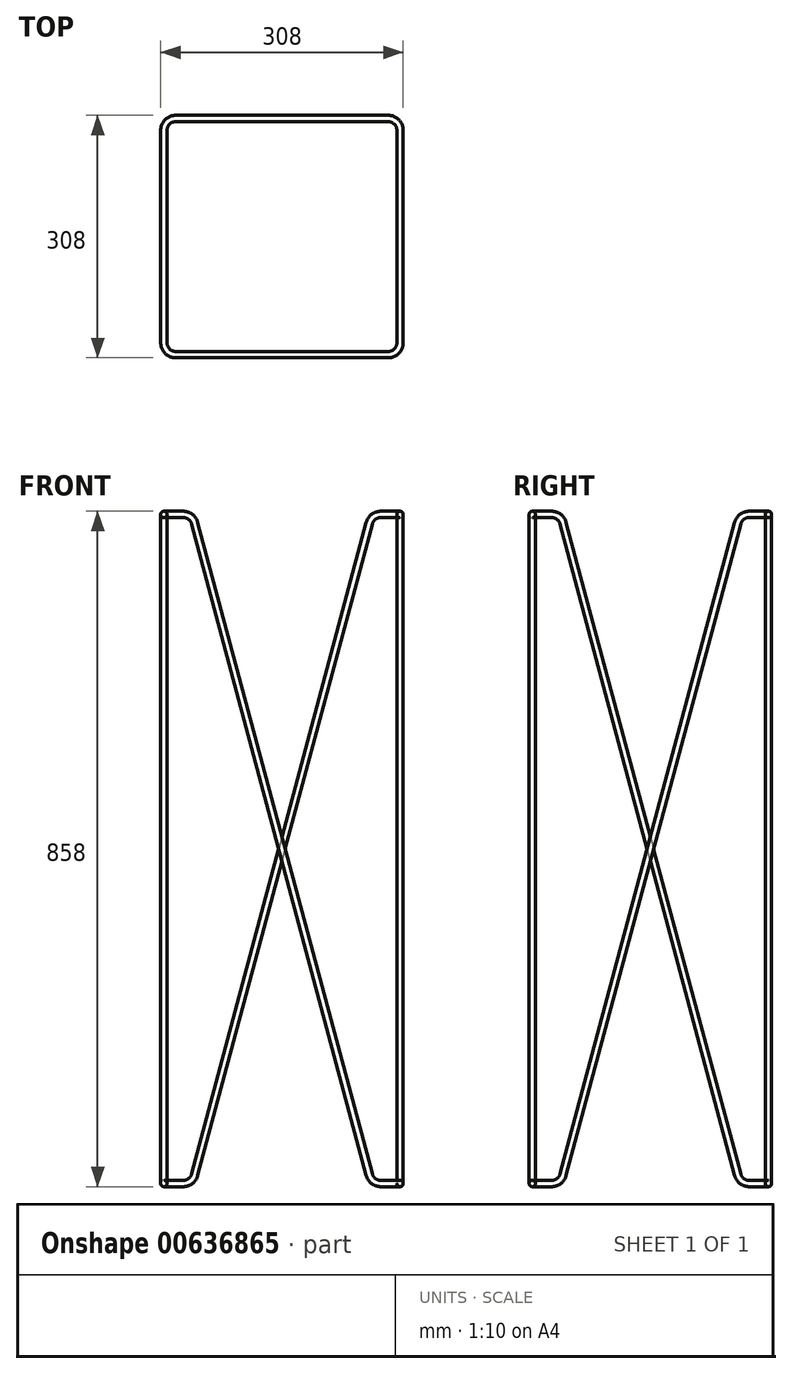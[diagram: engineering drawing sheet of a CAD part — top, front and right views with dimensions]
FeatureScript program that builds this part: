
annotation { "Feature Type Name" : "Feature", "Feature Type Description" : "" }
export const myFeature = defineFeature(function(context is Context, id is Id, definition is map)
    precondition{}
    {
        {
            var Q0;
            Q0=qCreatedBy(makeId("Top.planeOp"),FACE);
            var sketch = newSketch(context, id + "F0", { "sketchPlane" : qUnion([Q0])});
            skLineSegment(sketch, "E0.bottom", {"start": v(0, 0) * mm, "end": v(300, 0) * mm, "construction": true});
            skLineSegment(sketch, "E0.top", {"start": v(0, 300) * mm, "end": v(300, 300) * mm, "construction": true});
            skLineSegment(sketch, "E0.left", {"start": v(0, 0) * mm, "end": v(0, 300) * mm, "construction": true});
            skLineSegment(sketch, "E0.right", {"start": v(300, 0) * mm, "end": v(300, 300) * mm, "construction": true});
            skLineSegment(sketch, "E1", {"start": v(0, 300) * mm, "end": v(300, 0) * mm, "construction": true});
            skSolve(sketch);
        }
        {
            var Q0;
            Q0=sQuery(id+"F0.wireOp",EDGE,"E1");
            cPlane(context, id + "F1", {"entities" : qUnion([Q0]), "cplaneType" : CPlaneType.LINE_ANGLE, "offset" : 25 * mm, "angle" : 90 * degree, "oppositeDirection" : true, "width" : 150 * mm, "height" : 150 * mm});
        }
        {
            var Q0;
            Q0=qCreatedBy(makeId("Right.planeOp"),FACE);
            var sketch = newSketch(context, id + "F2", { "sketchPlane" : qUnion([Q0])});
            skLineSegment(sketch, "E2", {"start": v(0, 850) * mm, "end": v(24.61, 850) * mm, "construction": true});
            skLineSegment(sketch, "E3", {"start": v(39.1, 838.88) * mm, "end": v(260.9, 11.12) * mm});
            skLineSegment(sketch, "E4", {"start": v(275.39, 0) * mm, "end": v(300, 0) * mm, "construction": true});
            skLineSegment(sketch, "E5", {"start": v(0, 850) * mm, "end": v(0, 0) * mm, "construction": true});
            skPoint(sketch, "E6.visualSharp", {"position": v(36.12, 850) * mm});
            skArc(sketch, "E6.filletArc", {"start": v(39.1, 838.88) * mm, "mid": v(33.74, 846.9) * mm, "end": v(24.61, 850) * mm});
            skPoint(sketch, "E7.visualSharp", {"position": v(263.88, 0) * mm});
            skArc(sketch, "E7.filletArc", {"start": v(260.9, 11.12) * mm, "mid": v(266.26, 3.1) * mm, "end": v(275.39, 0) * mm});
            skSolve(sketch);
        }
        {
            var Q0;
            Q0=qCreatedBy(makeId("Front.planeOp"),FACE);
            var sketch = newSketch(context, id + "F3", { "sketchPlane" : qUnion([Q0])});
            skLineSegment(sketch, "E8.bottom", {"start": v(0, 0) * mm, "end": v(300, 0) * mm, "construction": true});
            skLineSegment(sketch, "E9", {"start": v(0, 850) * mm, "end": v(24.61, 850) * mm, "construction": true});
            skLineSegment(sketch, "E10", {"start": v(39.1, 838.88) * mm, "end": v(260.9, 11.12) * mm});
            skLineSegment(sketch, "E11", {"start": v(275.39, 0) * mm, "end": v(300, 0) * mm, "construction": true});
            skPoint(sketch, "E12.visualSharp", {"position": v(36.12, 850) * mm});
            skArc(sketch, "E12.filletArc", {"start": v(39.1, 838.88) * mm, "mid": v(33.74, 846.9) * mm, "end": v(24.61, 850) * mm});
            skPoint(sketch, "E13.visualSharp", {"position": v(263.88, 0) * mm});
            skArc(sketch, "E13.filletArc", {"start": v(260.9, 11.12) * mm, "mid": v(266.26, 3.1) * mm, "end": v(275.39, 0) * mm});
            skSolve(sketch);
        }
        {
            var Q0;
            Q0=qCreatedBy(makeId("Top.planeOp"),FACE);
            var Q1;
            Q1=sQuery(id+"F2.wireOp",VERTEX,"E5.start");
            cPlane(context, id + "F4", {"entities" : qUnion([Q0, Q1]), "cplaneType" : CPlaneType.PLANE_POINT, "offset" : 25 * mm, "width" : 150 * mm, "height" : 150 * mm});
        }
        {
            var Q0;
            Q0=qCreatedBy(id+"F4.planeOp",FACE);
            var sketch = newSketch(context, id + "F5", { "sketchPlane" : qUnion([Q0])});
            skLineSegment(sketch, "E14", {"start": v(0, 24.61) * mm, "end": v(0, 15) * mm});
            skLineSegment(sketch, "E15", {"start": v(15, 0) * mm, "end": v(24.61, 0) * mm});
            skPoint(sketch, "E16.visualSharp", {"position": v(0, 0) * mm});
            skArc(sketch, "E16.filletArc", {"start": v(0, 15) * mm, "mid": v(4.4, 4.4) * mm, "end": v(15, 0) * mm});
            skSolve(sketch);
        }
        {
            var Q0;
            Q0=qCreatedBy(makeId("Top.planeOp"),FACE);
            var sketch = newSketch(context, id + "F6", { "sketchPlane" : qUnion([Q0])});
            skLineSegment(sketch, "E17", {"start": v(0, 275.39) * mm, "end": v(0, 285) * mm});
            skPoint(sketch, "E18.visualSharp", {"position": v(0, 300) * mm});
            skArc(sketch, "E18.filletArc", {"start": v(4.4, 295.6) * mm, "mid": v(1.14, 290.74) * mm, "end": v(0, 285) * mm});
            skLineSegment(sketch, "E19", {"start": v(275.39, 0) * mm, "end": v(285, 0) * mm});
            skArc(sketch, "E20", {"start": v(285, 0) * mm, "mid": v(290.74, 1.14) * mm, "end": v(295.6, 4.4) * mm});
            skSolve(sketch);
        }
        {
            var Q0;
            Q0=qCreatedBy(id+"F1.planeOp",FACE);
            var sketch = newSketch(context, id + "F7", { "sketchPlane" : qUnion([Q0])});
            skCircle(sketch, "E21", {"center": v(205.92, 0) * mm, "radius": 4 * mm});
            skSolve(sketch);
        }
        {
            var Q0;
            Q0=makeQuery(id+"F7.imprint","IMPRINT",FACE,{"disambiguationData":[TD([[makeQuery(id+"F7.imprint","IMPRINT",EDGE,{"derivedFrom":sQuery(id+"F7.wireOp",EDGE,"E21")}),1.0]])]});
            var Q1;
            Q1=sQuery(id+"F6.wireOp",EDGE,"E20");
            var Q2;
            Q2=sQuery(id+"F6.wireOp",EDGE,"E19");
            var Q3;
            Q3=sQuery(id+"F3.wireOp",EDGE,"E13.filletArc");
            var Q4;
            Q4=sQuery(id+"F3.wireOp",EDGE,"E10");
            var Q5;
            Q5=sQuery(id+"F3.wireOp",EDGE,"E12.filletArc");
            var Q6;
            Q6=sQuery(id+"F5.wireOp",EDGE,"E15");
            var Q7;
            Q7=sQuery(id+"F5.wireOp",EDGE,"E16.filletArc");
            var Q8;
            Q8=sQuery(id+"F5.wireOp",EDGE,"E14");
            var Q9;
            Q9=sQuery(id+"F2.wireOp",EDGE,"E6.filletArc");
            var Q10;
            Q10=sQuery(id+"F2.wireOp",EDGE,"E3");
            var Q11;
            Q11=sQuery(id+"F2.wireOp",EDGE,"E7.filletArc");
            var Q12;
            Q12=sQuery(id+"F6.wireOp",EDGE,"E17");
            var Q13;
            Q13=sQuery(id+"F6.wireOp",EDGE,"E18.filletArc");
            sweep(context, id + "F8", {"profiles" : qUnion([Q0]), "path" : qUnion([Q1, Q2, Q3, Q4, Q5, Q6, Q7, Q8, Q9, Q10, Q11, Q12, Q13])});
        }
        {
            var Q0;
            Q0=makeQuery(id+"F8.opSweep","SWEPT_BODY",BODY,{"disambiguationData":[OSD([sQuery(id+"F6.wireOp",EDGE,"E18.filletArc"),sQuery(id+"F7.wireOp",EDGE,"E21")])]});
            var Q1;
            Q1=qCreatedBy(id+"F1.planeOp",FACE);
            mirror(context, id + "F9", {"operationType" : NewBodyOperationType.ADD, "entities" : qUnion([Q0]), "mirrorPlane" : qUnion([Q1])});
        }
    });
